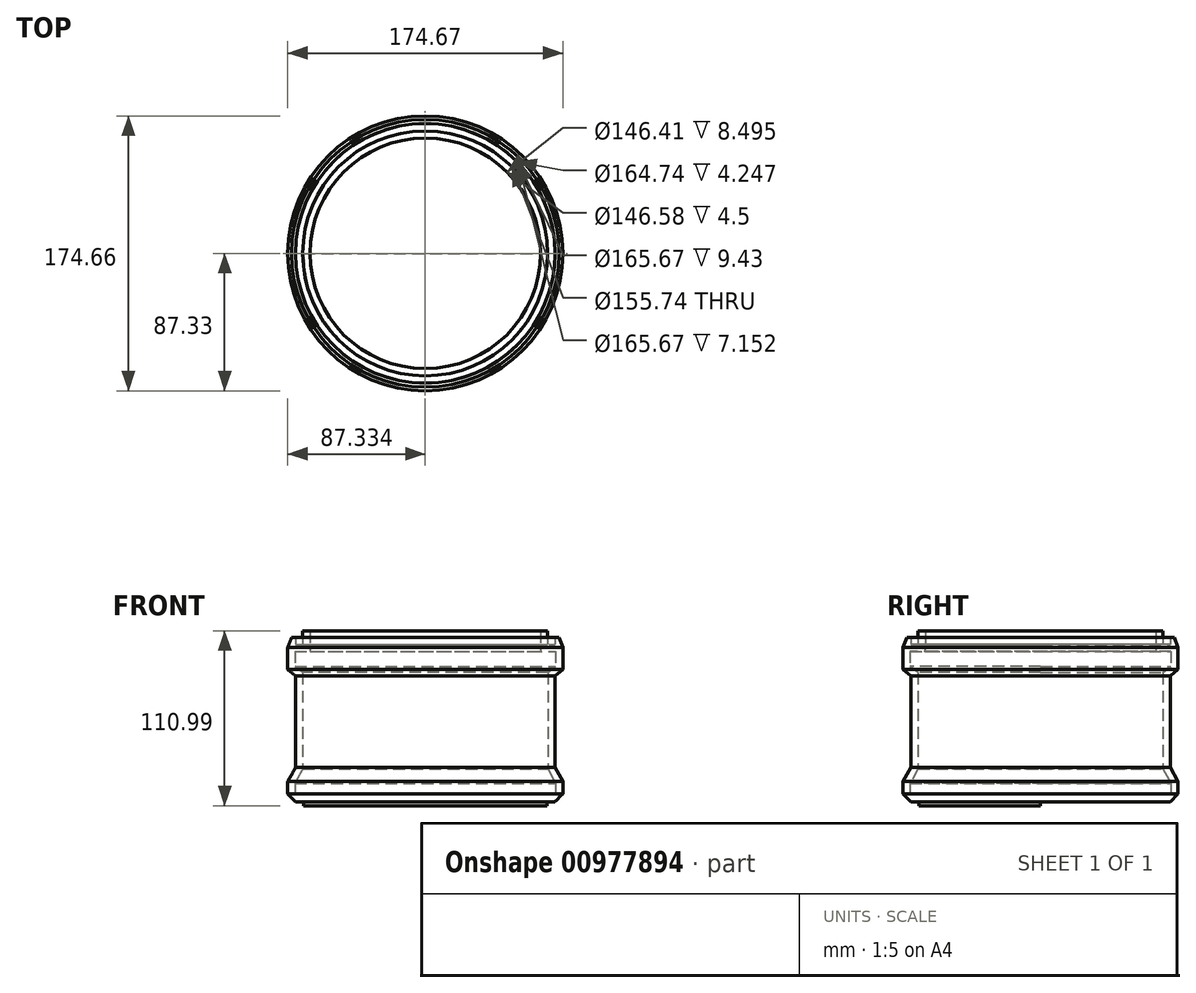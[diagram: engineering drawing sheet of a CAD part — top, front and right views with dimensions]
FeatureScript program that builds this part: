
annotation { "Feature Type Name" : "Feature", "Feature Type Description" : "" }
export const myFeature = defineFeature(function(context is Context, id is Id, definition is map)
    precondition{}
    {
        {
            var Q0;
            Q0=qCreatedBy(makeId("Front.planeOp"),FACE);
            var sketch = newSketch(context, id + "F0", { "sketchPlane" : qUnion([Q0])});
            skLineSegment(sketch, "E0", {"start": v(9.32, 56.9) * mm, "end": v(-63.88, 56.9) * mm});
            skLineSegment(sketch, "E1", {"start": v(-63.88, 56.9) * mm, "end": v(-63.88, 65.4) * mm});
            skLineSegment(sketch, "E2", {"start": v(-63.88, 65.4) * mm, "end": v(-68.47, 65.4) * mm});
            skLineSegment(sketch, "E3", {"start": v(-68.47, 65.4) * mm, "end": v(-68.47, 56.9) * mm});
            skLineSegment(sketch, "E4", {"start": v(-68.47, 56.9) * mm, "end": v(-73.05, 56.9) * mm});
            skLineSegment(sketch, "E5", {"start": v(-73.05, 56.9) * mm, "end": v(-73.05, 61.16) * mm});
            skPoint(sketch, "E5.endSnap0", {"position": v(-68.47, 61.16) * mm});
            skLineSegment(sketch, "E6", {"start": v(-73.05, 61.16) * mm, "end": v(-75.65, 61.16) * mm});
            skLineSegment(sketch, "E7", {"start": v(-75.65, 61.16) * mm, "end": v(-78, 55.02) * mm});
            skLineSegment(sketch, "E8", {"start": v(-78, 55.02) * mm, "end": v(-78, 40.86) * mm});
            skLineSegment(sketch, "E9", {"start": v(-78, 40.86) * mm, "end": v(-73.05, 36.77) * mm});
            skLineSegment(sketch, "E10", {"start": v(-73.05, 36.77) * mm, "end": v(-73.05, -21.22) * mm});
            skLineSegment(sketch, "E11", {"start": v(-73.05, -21.22) * mm, "end": v(-78, -30.29) * mm});
            skLineSegment(sketch, "E12", {"start": v(-78, -30.29) * mm, "end": v(-78, -43.1) * mm});
            skLineSegment(sketch, "E13", {"start": v(-78, -43.1) * mm, "end": v(9.32, -43.1) * mm});
            skLineSegment(sketch, "E14", {"start": v(9.32, -43.1) * mm, "end": v(9.32, 56.9) * mm});
            skSolve(sketch);
        }
        {
            var Q0;
            Q0 = qSketchRegion(id + "F0", true);
            var Q1;
            Q1=sQuery(id+"F0.wireOp",EDGE,"E14");
            revolve(context, id + "F1", {"surfaceOperationType" : NewSurfaceOperationType.NEW, "entities" : qUnion([Q0]), "axis" : qUnion([Q1]), "revolveType" : RevolveType.FULL});
        }
        {
            var Q0;
            Q0=makeQuery(id+"F1.opRevolve","SWEPT_FACE",FACE,{"disambiguationData":[OSD([sQuery(id+"F0.wireOp",EDGE,"E0")])]});
            shell(context, id + "F2", {"entities" : qUnion([Q0]), "thickness" : 4.5 * mm});
        }
        {
            var Q0;
            Q0=makeQuery(id+"F1.opRevolve","SWEPT_FACE",FACE,{"disambiguationData":[OSD([sQuery(id+"F0.wireOp",EDGE,"E13")])]});
            var sketch = newSketch(context, id + "F3", { "sketchPlane" : qUnion([Q0])});
            skLineSegment(sketch, "E15", {"start": v(-78, 0) * mm, "end": v(96.66, 0) * mm});
            skLineSegment(sketch, "E16", {"start": v(9.32, 87.33) * mm, "end": v(9.32, 0) * mm});
            skCircle(sketch, "E17", {"center": v(9.32, 0) * mm, "radius": 77.39 * mm});
            skCircle(sketch, "E18", {"center": v(9.32, 77.39) * mm, "radius": 5 * mm});
            skSolve(sketch);
        }
        {
            var Q0;
            {var subQ0=sQuery(id+"F3.wireOp",EDGE,"E18");var subQ1=sQuery(id+"F3.wireOp",EDGE,"E16");var subQ2=makeQuery(id+"F3.imprint","INTERSECT",VERTEX,{"disambiguationData":[OD(0.0)],"derivedFrom":[subQ1,subQ0]});Q0=makeQuery(id+"F3.imprint","IMPRINT",FACE,{"disambiguationData":[TD([[makeQuery(id+"F3.imprint","IMPRINT",EDGE,{"disambiguationData":[TD([[subQ2,-1.0]])],"derivedFrom":subQ1}),1.0]])]});}
            var Q1;
            {var subQ0=sQuery(id+"F3.wireOp",EDGE,"E17");var subQ1=sQuery(id+"F3.wireOp",EDGE,"E16");var subQ2=makeQuery(id+"F3.imprint","INTERSECT",VERTEX,{"derivedFrom":[subQ1,subQ0]});Q1=makeQuery(id+"F3.imprint","IMPRINT",FACE,{"disambiguationData":[TD([[makeQuery(id+"F3.imprint","IMPRINT",EDGE,{"disambiguationData":[TD([[subQ2,-1.0]])],"derivedFrom":subQ1}),1.0]])]});}
            var Q2;
            {var subQ0=sQuery(id+"F3.wireOp",EDGE,"E17");var subQ1=sQuery(id+"F3.wireOp",EDGE,"E16");var subQ2=makeQuery(id+"F3.imprint","INTERSECT",VERTEX,{"derivedFrom":[subQ1,subQ0]});Q2=makeQuery(id+"F3.imprint","IMPRINT",FACE,{"disambiguationData":[TD([[makeQuery(id+"F3.imprint","IMPRINT",EDGE,{"disambiguationData":[TD([[subQ2,-1.0]])],"derivedFrom":subQ1}),-1.0]])]});}
            var Q3;
            {var subQ0=sQuery(id+"F3.wireOp",EDGE,"E18");var subQ1=sQuery(id+"F3.wireOp",EDGE,"E16");var subQ2=makeQuery(id+"F3.imprint","INTERSECT",VERTEX,{"disambiguationData":[OD(0.0)],"derivedFrom":[subQ1,subQ0]});Q3=makeQuery(id+"F3.imprint","IMPRINT",FACE,{"disambiguationData":[TD([[makeQuery(id+"F3.imprint","IMPRINT",EDGE,{"disambiguationData":[TD([[subQ2,-1.0]])],"derivedFrom":subQ1}),-1.0]])]});}
            var Q4;
            Q4=sQuery(id+"F3.wireOp",EDGE,"E18");
            extrude(context, id + "F4", {"entities" : qUnion([Q0, Q1, Q2, Q3]), "operationType" : NewBodyOperationType.ADD, "surfaceEntities" : qUnion([Q4]), "depth" : 2.5 * mm, "offsetDistance" : 25 * mm});
        }
        {
            var Q0;
            Q0=makeQuery(id+"F1.opRevolve","SWEPT_EDGE",EDGE,{"disambiguationData":[OSD([sQuery(id+"F0.wireOp",EDGE,"E12"),sQuery(id+"F0.wireOp",EDGE,"E13")])]});
            chamfer(context, id + "F5", {"entities" : qUnion([Q0]), "width" : 5 * mm, "tangentPropagation" : true});
        }
    });
